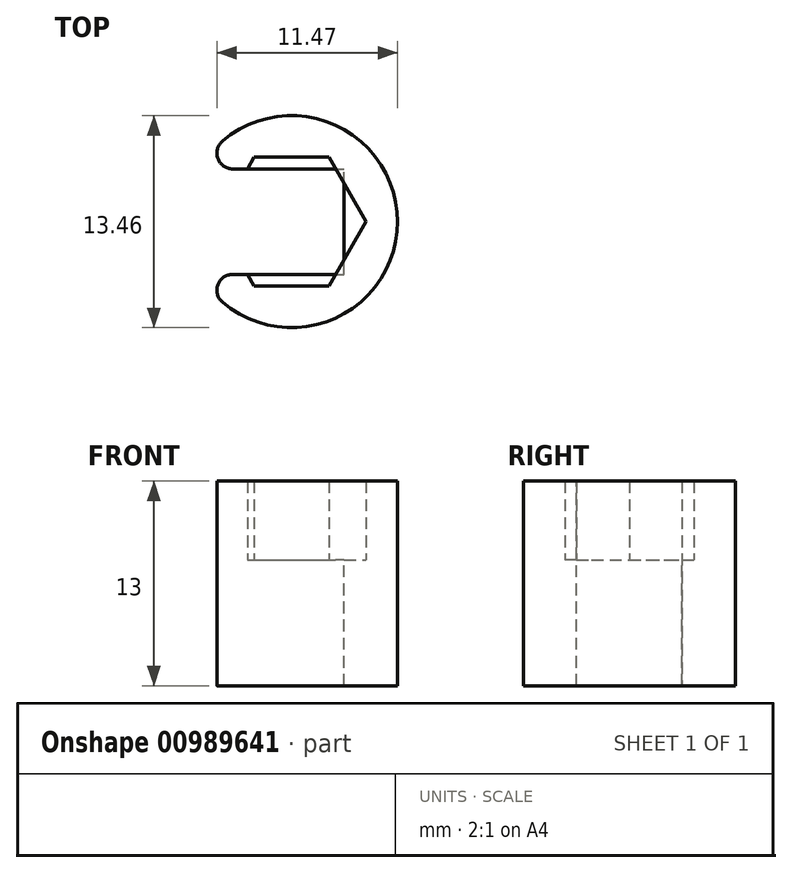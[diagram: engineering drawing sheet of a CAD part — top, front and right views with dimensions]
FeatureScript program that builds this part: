
annotation { "Feature Type Name" : "Feature", "Feature Type Description" : "" }
export const myFeature = defineFeature(function(context is Context, id is Id, definition is map)
    precondition{}
    {
        {
            var Q0;
            Q0=qCreatedBy(makeId("Top.planeOp"),FACE);
            var sketch = newSketch(context, id + "F0", { "sketchPlane" : qUnion([Q0])});
            skCircle(sketch, "E0.cCircle", {"center": v(0, 0) * mm, "radius": 4.1 * mm, "construction": true});
            skLineSegment(sketch, "E0.0", {"start": v(-2.37, 4.1) * mm, "end": v(2.37, 4.1) * mm});
            skLineSegment(sketch, "E0.1", {"start": v(2.37, 4.1) * mm, "end": v(4.73, 0) * mm});
            skLineSegment(sketch, "E0.2", {"start": v(4.73, 0) * mm, "end": v(2.37, -4.1) * mm});
            skLineSegment(sketch, "E0.3", {"start": v(2.37, -4.1) * mm, "end": v(-2.37, -4.1) * mm});
            skLineSegment(sketch, "E0.4", {"start": v(-2.37, -4.1) * mm, "end": v(-4.73, 0) * mm});
            skLineSegment(sketch, "E0.5", {"start": v(-4.73, 0) * mm, "end": v(-2.37, 4.1) * mm});
            skPoint(sketch, "E0.0.midPoint", {"position": v(0, 4.1) * mm});
            skCircle(sketch, "E1", {"center": v(0, 0) * mm, "radius": 6.73 * mm});
            skLineSegment(sketch, "E2", {"start": v(2.8, 3.35) * mm, "end": v(5.84, 3.35) * mm});
            skLineSegment(sketch, "E3", {"start": v(2.8, -3.35) * mm, "end": v(5.84, -3.35) * mm});
            skSolve(sketch);
        }
        {
            var Q0;
            {var subQ4=sQuery(id+"F0.wireOp",EDGE,"E0.0");Q0=makeQuery(id+"F0.imprint","IMPRINT",FACE,{"disambiguationData":[TD([[makeQuery(id+"F0.imprint","IMPRINT",EDGE,{"derivedFrom":subQ4}),1.0]])]});}
            extrude(context, id + "F1", {"entities" : qUnion([Q0]), "oppositeDirection" : true, "depth" : 5 * mm, "offsetDistance" : 25 * mm});
        }
        {
            var Q0;
            Q0=qCreatedBy(makeId("Top.planeOp"),FACE);
            var sketch = newSketch(context, id + "F2", { "sketchPlane" : qUnion([Q0])});
            skLineSegment(sketch, "E4.bottom", {"start": v(3.35, -3.35) * mm, "end": v(-3.35, -3.35) * mm});
            skLineSegment(sketch, "E4.top", {"start": v(3.35, 3.35) * mm, "end": v(-3.35, 3.35) * mm});
            skLineSegment(sketch, "E4.left", {"start": v(3.35, -3.35) * mm, "end": v(3.35, 3.35) * mm});
            skLineSegment(sketch, "E4.right", {"start": v(-3.35, -3.35) * mm, "end": v(-3.35, 3.35) * mm});
            skPoint(sketch, "E4.middle", {"position": v(0, 0) * mm});
            skCircle(sketch, "E5", {"center": v(0, 0) * mm, "radius": 6.73 * mm});
            skLineSegment(sketch, "E6", {"start": v(3.35, 3.35) * mm, "end": v(5.84, 3.35) * mm});
            skLineSegment(sketch, "E7", {"start": v(3.35, -3.35) * mm, "end": v(5.84, -3.35) * mm});
            skSolve(sketch);
        }
        {
            var Q0;
            Q0=makeQuery(id+"F2.imprint","IMPRINT",FACE,{"disambiguationData":[TD([[makeQuery(id+"F2.imprint","IMPRINT",EDGE,{"derivedFrom":sQuery(id+"F2.wireOp",EDGE,"E4.bottom")}),1.0]])]});
            extrude(context, id + "F3", {"entities" : qUnion([Q0]), "operationType" : NewBodyOperationType.ADD, "depth" : 8 * mm, "offsetDistance" : 25 * mm});
        }
        {
            var Q0;
            Q0=makeQuery(id+"F3.boolean.opBoolean","MERGE",EDGE,{"derivedFrom":[makeQuery(id+"F1.opExtrude","SWEPT_EDGE",EDGE,{"disambiguationData":[OSD([sQuery(id+"F0.wireOp",EDGE,"E1"),sQuery(id+"F0.wireOp",EDGE,"E2")])]}),makeQuery(id+"F3.opExtrude","SWEPT_EDGE",EDGE,{"disambiguationData":[OSD([sQuery(id+"F2.wireOp",EDGE,"E5"),sQuery(id+"F2.wireOp",EDGE,"E6")])]})]});
            var Q1;
            Q1=makeQuery(id+"F3.boolean.opBoolean","MERGE",EDGE,{"derivedFrom":[makeQuery(id+"F1.opExtrude","SWEPT_EDGE",EDGE,{"disambiguationData":[OSD([sQuery(id+"F0.wireOp",EDGE,"E1"),sQuery(id+"F0.wireOp",EDGE,"E3")])]}),makeQuery(id+"F3.opExtrude","SWEPT_EDGE",EDGE,{"disambiguationData":[OSD([sQuery(id+"F2.wireOp",EDGE,"E5"),sQuery(id+"F2.wireOp",EDGE,"E7")])]})]});
            fillet(context, id + "F4", {"entities" : qUnion([Q0, Q1]), "tangentPropagation" : true, "radius" : 1 * mm, "defaultsChanged" : true, "vertexSettings" : [], "allowEdgeOverflow" : false});
        }
        {
            var Q0;
            Q0=makeQuery(id+"F1.opExtrude","SWEPT_BODY",BODY,{"disambiguationData":[OSD([sQuery(id+"F0.wireOp",EDGE,"E0.0"),sQuery(id+"F0.wireOp",EDGE,"E0.1"),sQuery(id+"F0.wireOp",EDGE,"E0.2"),sQuery(id+"F0.wireOp",EDGE,"E0.3"),sQuery(id+"F0.wireOp",EDGE,"E0.4"),sQuery(id+"F0.wireOp",EDGE,"E0.5"),sQuery(id+"F0.wireOp",EDGE,"E1"),sQuery(id+"F0.wireOp",EDGE,"E2"),sQuery(id+"F0.wireOp",EDGE,"E3")])]});
            var Q1;
            Q1=makeQuery(id+"F3.opExtrude","CAP_EDGE",EDGE,{"disambiguationData":[OSD([sQuery(id+"F2.wireOp",EDGE,"E4.right")])],"isStart":false});
            transform(context, id + "F5", {"entities" : qUnion([Q0]), "transformType" : TransformType.ROTATION, "transformAxis" : qUnion([Q1]), "angle" : 180 * degree, "makeCopy" : false});
        }
    });
